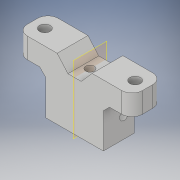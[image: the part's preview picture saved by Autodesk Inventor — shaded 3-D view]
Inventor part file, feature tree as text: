
AUTODESK INVENTOR PART (.ipt)
format: ipt  version: 2018 (Build 220112000, 112)  size: 197,120 bytes
history: native  units: in
note: dims shown in document units (in); Inventor stores cm internally (conversion verified against a paired STEP export)
features: extrude x7, sketch x7, mirror x1, fillet x1, chamfer x1
ambient origin geometry x8: Origin, YZ Plane, XZ Plane, XY Plane, X Axis, Y Axis, Z Axis, Center Point
bodies: Solid1 (feature_tree)
feature tree (17):
  extrude  "Extrusion1"  Depth=0.7874in
  extrude  "Extrusion2"  Depth=0.1575in
  extrude  "Extrusion3"  Depth=0.3937in
  mirror  "Mirror1"
  extrude  "Extrusion4"  Depth=0.5906in
  extrude  "Extrusion5"  Depth=0.2362in
  extrude  "Extrusion6"  Depth=0.3228in
  fillet  "Fillet1"  Radius=0.1969in
  chamfer  "Chamfer1"  Distance=0.3228in
  extrude  "Extrusion7"  Depth=0.1181in
  sketch  "Sketch1"  dims[d0=0.7874in d1=0.7874in]
  sketch  "Sketch2"  dims[d2=0.1575in d3=0.1575in]
  sketch  "Sketch3"  dims[d4=0.5512in d5=0.3937in]
  sketch  "Sketch4"  dims[d6=0.5906in d7=0.0in d8=0.2047in]
  sketch  "Sketch6"  dims[d9=0.2362in d10=0.2362in]
  sketch  "Sketch7"  dims[d11=0.3937in d12=0.0in d13=0.3228in d17=0.1969in d18=0.0in]
  sketch  "Sketch8"  dims[d22=0.3504in d23=0.3228in d24=0.1654in d25=0.3937in d27=0.1969in d28=0.0in d29=0.2559in d30=0.6693in d31=0.1575in d32=0.1969in d33=0.0in d34=0.1654in d35=0.1969in d36=0.0in d37=0.1969in d38=0.1181in d39=0.0787in d40=45.0deg d41=0.1181in d42=0.0in]
